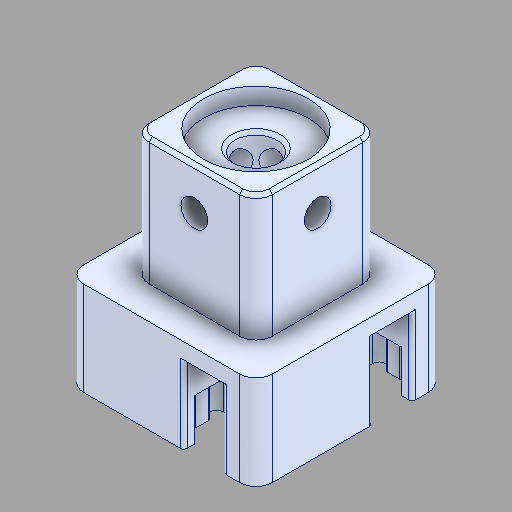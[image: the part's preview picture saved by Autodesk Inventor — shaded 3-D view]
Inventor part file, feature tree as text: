
AUTODESK INVENTOR PART (.ipt)
format: ipt  version: 2024.2 (Build 282272000, 272)  size: 254,464 bytes
history: native  units: in
note: dims shown in document units (in); Inventor stores cm internally (conversion verified against a paired STEP export)
features: fillet x1
ambient origin geometry x8: Origin, YZ Plane, XZ Plane, XY Plane, X Axis, Y Axis, Z Axis, Center Point
bodies: Solid1 (feature_tree)
feature tree (1):
  fillet  "Fillet11"  [1 undecoded]
note: 1 required parameter value undecoded (feature->parameter linkage not recoverable at this tier; creation-order binding heuristic only, values carry confidence <= 0.55)
